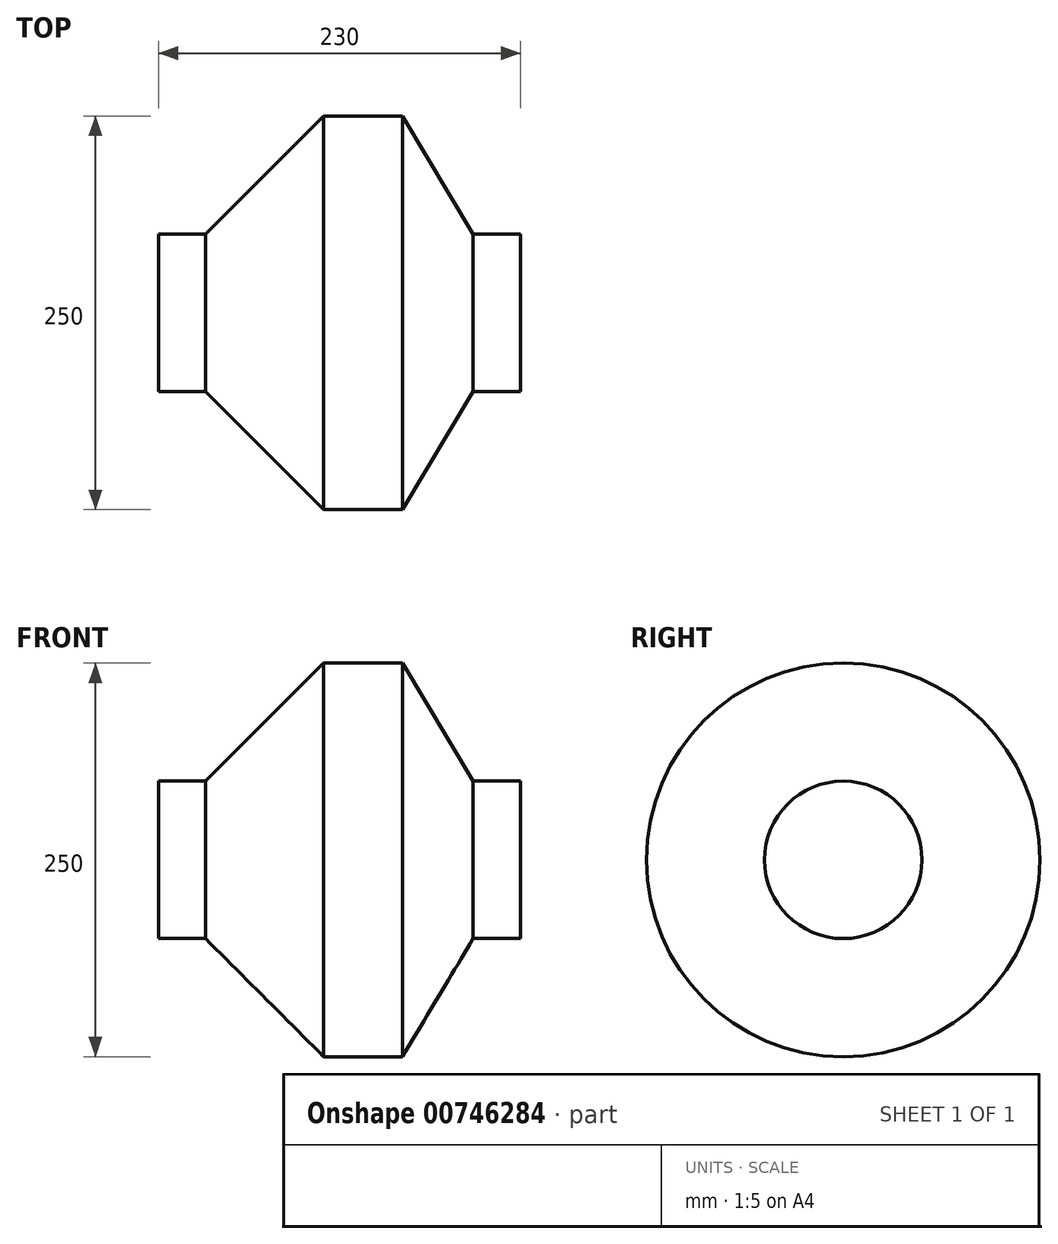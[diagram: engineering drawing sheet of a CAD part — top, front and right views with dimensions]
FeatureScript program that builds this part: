
annotation { "Feature Type Name" : "Feature", "Feature Type Description" : "" }
export const myFeature = defineFeature(function(context is Context, id is Id, definition is map)
    precondition{}
    {
        {
            var Q0;
            Q0=qCreatedBy(makeId("Top.planeOp"),FACE);
            var sketch = newSketch(context, id + "F0", { "sketchPlane" : qUnion([Q0])});
            skLineSegment(sketch, "E0", {"start": v(0, 0) * mm, "end": v(0, 50) * mm});
            skLineSegment(sketch, "E1", {"start": v(0, 50) * mm, "end": v(30, 50) * mm});
            skLineSegment(sketch, "E2", {"start": v(30, 50) * mm, "end": v(105, 125) * mm});
            skLineSegment(sketch, "E3", {"start": v(105, 125) * mm, "end": v(155, 125) * mm});
            skLineSegment(sketch, "E4", {"start": v(155, 125) * mm, "end": v(200, 50) * mm});
            skLineSegment(sketch, "E5", {"start": v(200, 50) * mm, "end": v(230, 50) * mm});
            skLineSegment(sketch, "E6", {"start": v(230, 50) * mm, "end": v(230, 0) * mm});
            skLineSegment(sketch, "E7", {"start": v(230, 0) * mm, "end": v(0, 0) * mm});
            skSolve(sketch);
        }
        {
            var Q0;
            Q0=makeQuery(id+"F0.imprint","IMPRINT",FACE,{"disambiguationData":[TD([[makeQuery(id+"F0.imprint","IMPRINT",EDGE,{"derivedFrom":sQuery(id+"F0.wireOp",EDGE,"E0")}),-1.0]])]});
            var Q1;
            Q1=sQuery(id+"F0.wireOp",EDGE,"E7");
            revolve(context, id + "F1", {"surfaceOperationType" : NewSurfaceOperationType.NEW, "entities" : qUnion([Q0]), "axis" : qUnion([Q1]), "revolveType" : RevolveType.FULL});
        }
    });
